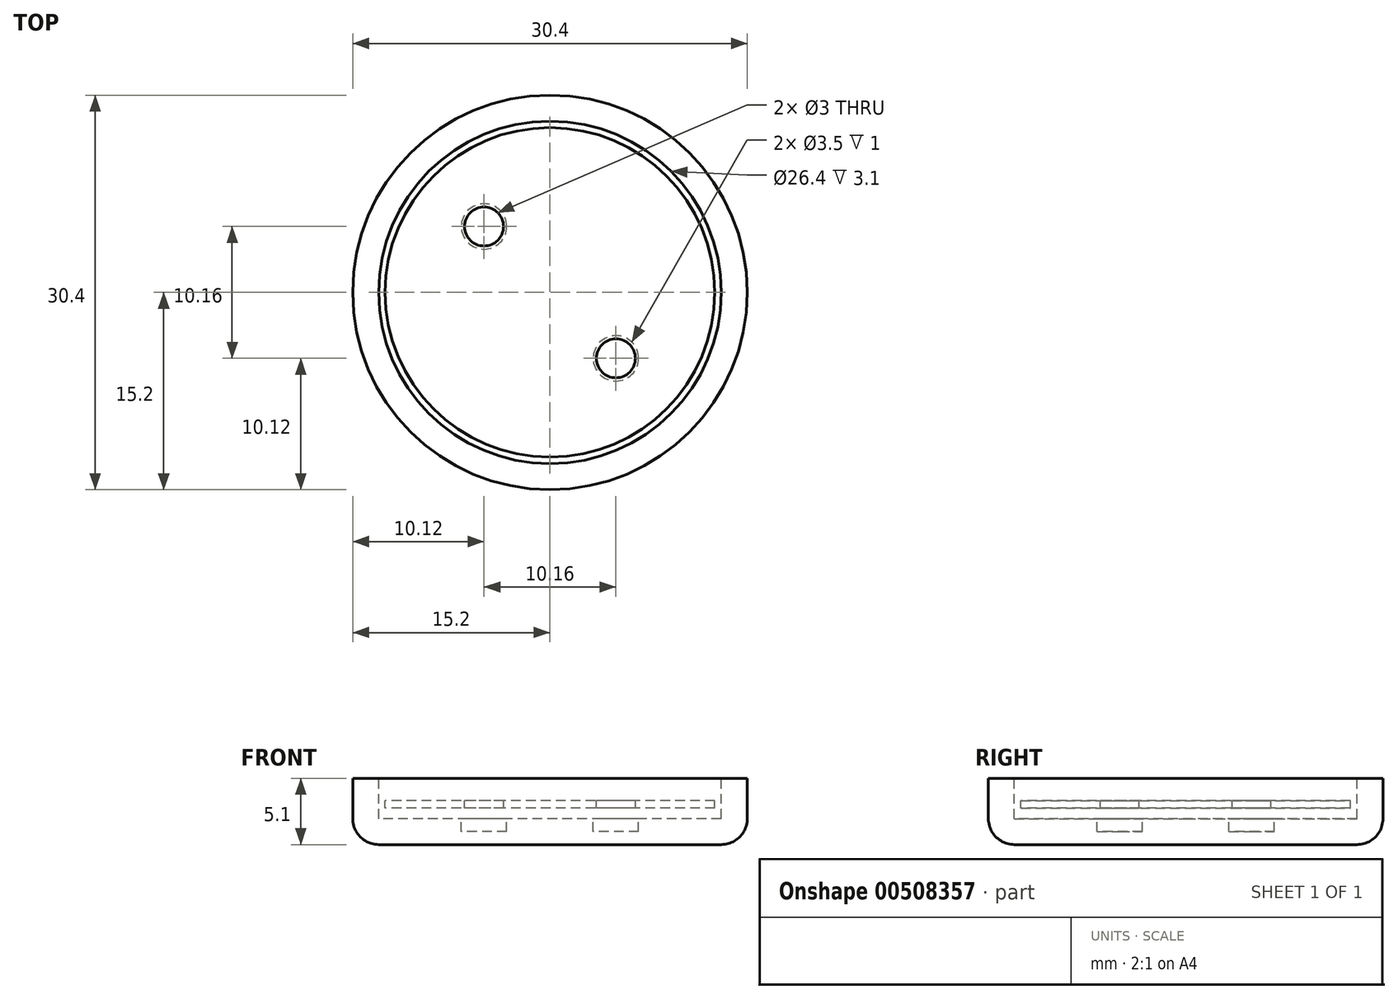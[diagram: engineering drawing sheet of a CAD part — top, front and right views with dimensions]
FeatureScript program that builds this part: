
annotation { "Feature Type Name" : "Feature", "Feature Type Description" : "" }
export const myFeature = defineFeature(function(context is Context, id is Id, definition is map)
    precondition{}
    {
        {
            var Q0;
            Q0=qCreatedBy(makeId("Top.planeOp"),FACE);
            var sketch = newSketch(context, id + "F0", { "sketchPlane" : qUnion([Q0])});
            skPoint(sketch, "E0.middle", {"position": v(0, 6) * mm});
            skArc(sketch, "E1", {"start": v(1, -11.88) * mm, "mid": v(0, 11.93) * mm, "end": v(-1, -11.88) * mm});
            skArc(sketch, "E2", {"start": v(-0.5, -11.41) * mm, "mid": v(1, 11.38) * mm, "end": v(-1.5, -11.33) * mm});
            skArc(sketch, "E3", {"start": v(-1, -10.88) * mm, "mid": v(1.5, 10.82) * mm, "end": v(-2, -10.74) * mm});
            skArc(sketch, "E4", {"start": v(-1.5, -10.32) * mm, "mid": v(2, 10.23) * mm, "end": v(-2.5, -10.12) * mm});
            skLineSegment(sketch, "E5", {"start": v(-1, -11.88) * mm, "end": v(-0.5, -11.41) * mm});
            skLineSegment(sketch, "E6", {"start": v(-1.5, -11.33) * mm, "end": v(-1, -10.88) * mm});
            skLineSegment(sketch, "E7", {"start": v(-2, -10.74) * mm, "end": v(-1.5, -10.32) * mm});
            skSolve(sketch);
        }
        {
            var Q0;
            Q0=qCreatedBy(makeId("Top.planeOp"),FACE);
            var sketch = newSketch(context, id + "F1", { "sketchPlane" : qUnion([Q0])});
            skCircle(sketch, "E8", {"center": v(0, 0) * mm, "radius": 12.7 * mm});
            skCircle(sketch, "E9", {"center": v(-5.08, 5.08) * mm, "radius": 1.5 * mm});
            skCircle(sketch, "E10", {"center": v(5.08, -5.08) * mm, "radius": 1.5 * mm});
            skSolve(sketch);
        }
        {
            var Q0;
            Q0=makeQuery(id+"F1.imprint","IMPRINT",FACE,{"disambiguationData":[TD([[makeQuery(id+"F1.imprint","IMPRINT",EDGE,{"derivedFrom":sQuery(id+"F1.wireOp",EDGE,"E8")}),1.0]])]});
            extrude(context, id + "F2", {"entities" : qUnion([Q0]), "oppositeDirection" : true, "depth" : 0.6 * mm, "offsetDistance" : 25 * mm});
        }
        {
            var Q0;
            Q0=qCreatedBy(makeId("Front.planeOp"),FACE);
            var sketch = newSketch(context, id + "F3", { "sketchPlane" : qUnion([Q0])});
            skLineSegment(sketch, "E11", {"start": v(0, -1.4) * mm, "end": v(13.2, -1.4) * mm});
            skLineSegment(sketch, "E12", {"start": v(13.2, -1.4) * mm, "end": v(13.2, 1.7) * mm});
            skLineSegment(sketch, "E13.0", {"start": v(15.2, -1.4) * mm, "end": v(15.2, 1.7) * mm});
            skLineSegment(sketch, "E13.1", {"start": v(0, -3.4) * mm, "end": v(13.2, -3.4) * mm});
            skLineSegment(sketch, "E14", {"start": v(13.2, 1.7) * mm, "end": v(15.2, 1.7) * mm});
            skLineSegment(sketch, "E15", {"start": v(0, -1.4) * mm, "end": v(0, -3.4) * mm});
            skPoint(sketch, "E16.visualSharp", {"position": v(15.2, -3.4) * mm});
            skArc(sketch, "E16.filletArc", {"start": v(13.2, -3.4) * mm, "mid": v(14.61, -2.81) * mm, "end": v(15.2, -1.4) * mm});
            skSolve(sketch);
        }
        {
            var Q0;
            Q0 = qSketchRegion(id + "F3", true);
            var Q1;
            Q1=sQuery(id+"F3.wireOp",EDGE,"E15");
            revolve(context, id + "F4", {"entities" : qUnion([Q0]), "axis" : qUnion([Q1]), "revolveType" : RevolveType.FULL});
        }
        {
            var Q0;
            Q0=makeQuery(id+"F4.opRevolve","SWEPT_FACE",FACE,{"disambiguationData":[OSD([sQuery(id+"F3.wireOp",EDGE,"E11")])]});
            var sketch = newSketch(context, id + "F5", { "sketchPlane" : qUnion([Q0])});
            skCircle(sketch, "E17", {"center": v(-5.08, 5.08) * mm, "radius": 1.75 * mm});
            skCircle(sketch, "E18", {"center": v(5.08, -5.08) * mm, "radius": 1.75 * mm});
            skSolve(sketch);
        }
        {
            var Q0;
            Q0=makeQuery(id+"F5.imprint","IMPRINT",FACE,{"disambiguationData":[TD([[makeQuery(id+"F5.imprint","IMPRINT",EDGE,{"derivedFrom":sQuery(id+"F5.wireOp",EDGE,"E17")}),1.0]])]});
            var Q1;
            Q1=makeQuery(id+"F5.imprint","IMPRINT",FACE,{"disambiguationData":[TD([[makeQuery(id+"F5.imprint","IMPRINT",EDGE,{"derivedFrom":sQuery(id+"F5.wireOp",EDGE,"E18")}),1.0]])]});
            extrude(context, id + "F6", {"entities" : qUnion([Q0, Q1]), "operationType" : NewBodyOperationType.REMOVE, "oppositeDirection" : true, "depth" : 1 * mm, "offsetDistance" : 25 * mm});
        }
    });
